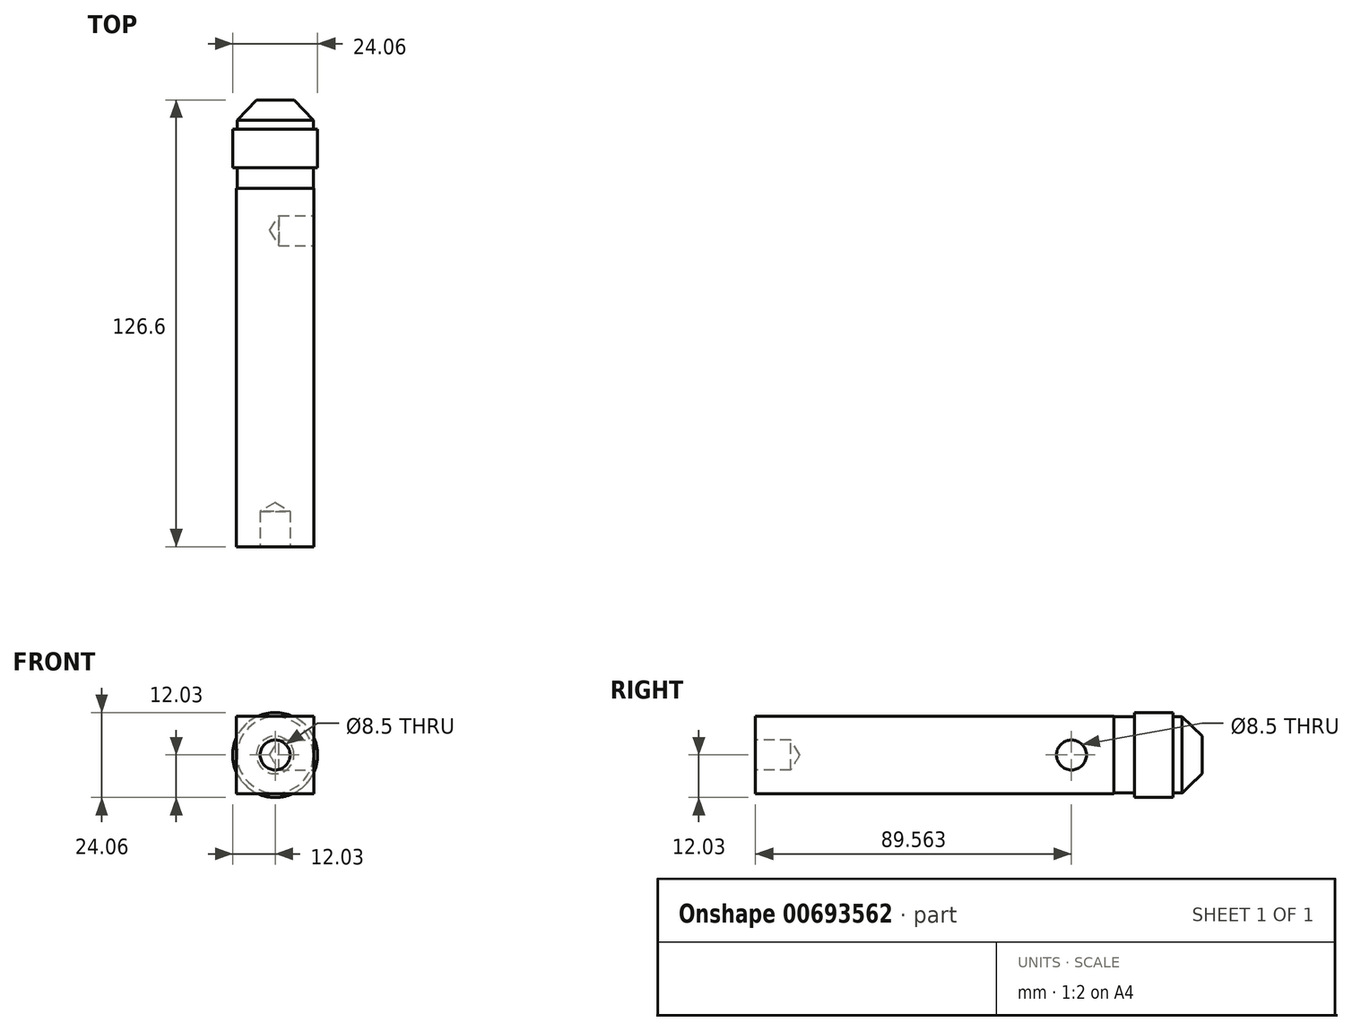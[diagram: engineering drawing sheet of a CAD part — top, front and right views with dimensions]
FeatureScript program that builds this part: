
annotation { "Feature Type Name" : "Feature", "Feature Type Description" : "" }
export const myFeature = defineFeature(function(context is Context, id is Id, definition is map)
    precondition{}
    {
        {
            var Q0;
            Q0=qCreatedBy(makeId("Front.planeOp"),FACE);
            var sketch = newSketch(context, id + "F0", { "sketchPlane" : qUnion([Q0])});
            skLineSegment(sketch, "E0.bottom", {"start": v(11, -11) * mm, "end": v(-11, -11) * mm});
            skLineSegment(sketch, "E0.top", {"start": v(11, 11) * mm, "end": v(-11, 11) * mm});
            skLineSegment(sketch, "E0.left", {"start": v(11, -11) * mm, "end": v(11, 11) * mm});
            skLineSegment(sketch, "E0.right", {"start": v(-11, -11) * mm, "end": v(-11, 11) * mm});
            skPoint(sketch, "E0.middle", {"position": v(0, 0) * mm});
            skSolve(sketch);
        }
        {
            var Q0;
            Q0 = qSketchRegion(id + "F0", true);
            extrude(context, id + "F1", {"entities" : qUnion([Q0]), "depth" : 101.6 * mm, "offsetDistance" : 25 * mm});
        }
        {
            var Q0;
            Q0=qCreatedBy(makeId("Top.planeOp"),FACE);
            var sketch = newSketch(context, id + "F2", { "sketchPlane" : qUnion([Q0])});
            skLineSegment(sketch, "E1", {"start": v(0, 0) * mm, "end": v(0, 25) * mm});
            skLineSegment(sketch, "E2", {"start": v(0, 25) * mm, "end": v(-5.33, 25) * mm});
            skLineSegment(sketch, "E3", {"start": v(-5.33, 25) * mm, "end": v(-10.8, 19.24) * mm});
            skLineSegment(sketch, "E4", {"start": v(-10.8, 19.24) * mm, "end": v(-10.8, 16.73) * mm});
            skLineSegment(sketch, "E5", {"start": v(-10.8, 16.73) * mm, "end": v(-12.03, 16.73) * mm});
            skLineSegment(sketch, "E6", {"start": v(-12.03, 16.73) * mm, "end": v(-12.03, 5.76) * mm});
            skLineSegment(sketch, "E7", {"start": v(-12.03, 5.76) * mm, "end": v(-10.8, 5.76) * mm});
            skLineSegment(sketch, "E8", {"start": v(-10.8, 5.76) * mm, "end": v(-10.8, 0) * mm});
            skLineSegment(sketch, "E9", {"start": v(-10.8, 0) * mm, "end": v(0, 0) * mm});
            skSolve(sketch);
        }
        {
            var Q0;
            Q0 = qSketchRegion(id + "F2", true);
            var Q1;
            Q1=sQuery(id+"F2.wireOp",EDGE,"E1");
            revolve(context, id + "F3", {"operationType" : NewBodyOperationType.ADD, "surfaceOperationType" : NewSurfaceOperationType.NEW, "entities" : qUnion([Q0]), "axis" : qUnion([Q1]), "revolveType" : RevolveType.FULL});
        }
        {
            var Q0;
            Q0=makeQuery(id+"F1.opExtrude","SWEPT_FACE",FACE,{"disambiguationData":[OSD([sQuery(id+"F0.wireOp",EDGE,"E0.left")])]});
            var sketch = newSketch(context, id + "F4", { "sketchPlane" : qUnion([Q0])});
            skPoint(sketch, "E10", {"position": v(-12.04, 0) * mm});
            skPoint(sketch, "E10.positionSnap0", {"position": v(0, 0) * mm});
            skSolve(sketch);
        }
        {
            var Q0;
            Q0=sQuery(id+"F4.wireOp",VERTEX,"E10");
            var Q1;
            Q1=makeQuery(id+"F1.opExtrude","SWEPT_BODY",BODY,{"disambiguationData":[OSD([sQuery(id+"F0.wireOp",EDGE,"E0.bottom"),sQuery(id+"F0.wireOp",EDGE,"E0.top"),sQuery(id+"F0.wireOp",EDGE,"E0.left"),sQuery(id+"F0.wireOp",EDGE,"E0.right")])]});
            hole(context, id + "F5", {"style" : HoleStyle.SIMPLE, "endStyle" : HoleEndStyle.BLIND, "holeDiameter" : 8.5 * mm, "majorDiameter" : 5 * mm, "holeDepth" : 10 * mm, "isTappedThrough" : true, "tappedDepth" : 12 * mm, "tapClearance" : 3, "startFromSketch" : true, "locations" : qUnion([Q0]), "scope" : qUnion([Q1])});
        }
        {
            var Q0;
            Q0=makeQuery(id+"F1.opExtrude","CAP_FACE",FACE,{"disambiguationData":[OSD([sQuery(id+"F0.wireOp",EDGE,"E0.bottom"),sQuery(id+"F0.wireOp",EDGE,"E0.top"),sQuery(id+"F0.wireOp",EDGE,"E0.left"),sQuery(id+"F0.wireOp",EDGE,"E0.right")])],"isStart":false});
            var sketch = newSketch(context, id + "F6", { "sketchPlane" : qUnion([Q0])});
            skPoint(sketch, "E11", {"position": v(0, 0) * mm});
            skPoint(sketch, "E11.positionSnap0", {"position": v(11, 0) * mm});
            skPoint(sketch, "E11.positionSnap1", {"position": v(0, 11) * mm});
            skSolve(sketch);
        }
        {
            var Q0;
            Q0=sQuery(id+"F6.wireOp",VERTEX,"E11");
            var Q1;
            Q1=makeQuery(id+"F1.opExtrude","SWEPT_BODY",BODY,{"disambiguationData":[OSD([sQuery(id+"F0.wireOp",EDGE,"E0.bottom"),sQuery(id+"F0.wireOp",EDGE,"E0.top"),sQuery(id+"F0.wireOp",EDGE,"E0.left"),sQuery(id+"F0.wireOp",EDGE,"E0.right")])]});
            hole(context, id + "F7", {"style" : HoleStyle.SIMPLE, "endStyle" : HoleEndStyle.BLIND, "holeDiameter" : 8.5 * mm, "majorDiameter" : 5 * mm, "holeDepth" : 10 * mm, "isTappedThrough" : true, "tappedDepth" : 12 * mm, "tapClearance" : 3, "startFromSketch" : true, "locations" : qUnion([Q0]), "scope" : qUnion([Q1])});
        }
    });
